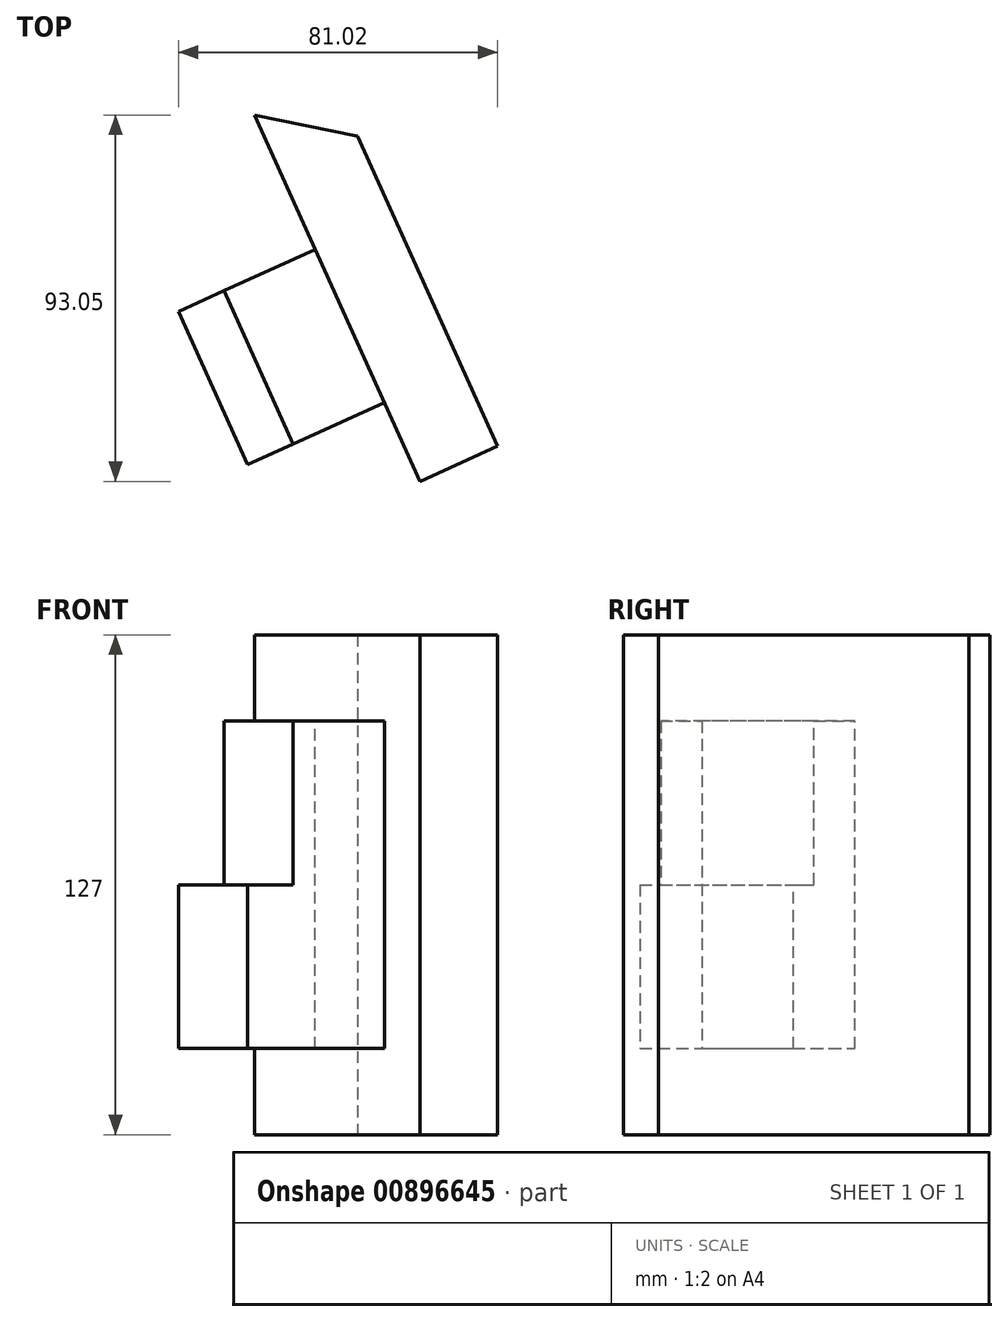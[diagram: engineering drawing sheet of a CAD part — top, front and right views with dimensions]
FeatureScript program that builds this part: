
annotation { "Feature Type Name" : "Feature", "Feature Type Description" : "" }
export const myFeature = defineFeature(function(context is Context, id is Id, definition is map)
    precondition{}
    {
        {
            var Q0;
            Q0=qCreatedBy(makeId("Top.planeOp"),FACE);
            var sketch = newSketch(context, id + "F0", { "sketchPlane" : qUnion([Q0])});
            skLineSegment(sketch, "E0", {"start": v(-10.82, 72.83) * mm, "end": v(31.2, -20.22) * mm});
            skLineSegment(sketch, "E1", {"start": v(31.2, -20.22) * mm, "end": v(50.91, -11.32) * mm});
            skLineSegment(sketch, "E2", {"start": v(50.91, -11.32) * mm, "end": v(15.33, 67.5) * mm});
            skLineSegment(sketch, "E3", {"start": v(15.33, 67.5) * mm, "end": v(-10.82, 72.83) * mm});
            skSolve(sketch);
        }
        {
            var Q0;
            Q0=makeQuery(id+"F0.imprint","IMPRINT",FACE,{"disambiguationData":[TD([[makeQuery(id+"F0.imprint","IMPRINT",EDGE,{"derivedFrom":sQuery(id+"F0.wireOp",EDGE,"E0")}),1.0]])]});
            extrude(context, id + "F1", {"entities" : qUnion([Q0]), "depth" : 127 * mm, "offsetDistance" : 25.4 * mm});
        }
        {
            var Q0;
            Q0=makeQuery(id+"F1.opExtrude","SWEPT_FACE",FACE,{"disambiguationData":[OSD([sQuery(id+"F0.wireOp",EDGE,"E0")])]});
            var sketch = newSketch(context, id + "F2", { "sketchPlane" : qUnion([Q0])});
            skLineSegment(sketch, "E4.0", {"start": v(9.38, 21.9) * mm, "end": v(-33.32, 21.9) * mm});
            skLineSegment(sketch, "E4.1", {"start": v(9.38, 105.1) * mm, "end": v(9.38, 21.9) * mm});
            skLineSegment(sketch, "E4.2", {"start": v(-33.32, 105.1) * mm, "end": v(9.38, 105.1) * mm});
            skLineSegment(sketch, "E4.3", {"start": v(-33.32, 21.9) * mm, "end": v(-33.32, 105.1) * mm});
            skSolve(sketch);
        }
        {
            var Q0;
            Q0=makeQuery(id+"F2.imprint","IMPRINT",FACE,{"disambiguationData":[TD([[makeQuery(id+"F2.imprint","IMPRINT",EDGE,{"derivedFrom":sQuery(id+"F2.wireOp",EDGE,"E4.0")}),-1.0]])]});
            extrude(context, id + "F3", {"entities" : qUnion([Q0]), "operationType" : NewBodyOperationType.ADD, "depth" : 25.4 * mm, "offsetDistance" : 25.4 * mm});
        }
        {
            var Q0;
            Q0=makeQuery(id+"F3.opExtrude","CAP_FACE",FACE,{"disambiguationData":[OSD([sQuery(id+"F2.wireOp",EDGE,"E4.0"),sQuery(id+"F2.wireOp",EDGE,"E4.1"),sQuery(id+"F2.wireOp",EDGE,"E4.2"),sQuery(id+"F2.wireOp",EDGE,"E4.3")])],"isStart":false});
            var sketch = newSketch(context, id + "F4", { "sketchPlane" : qUnion([Q0])});
            skLineSegment(sketch, "E5", {"start": v(9.38, 63.5) * mm, "end": v(-33.32, 63.5) * mm});
            skSolve(sketch);
        }
        {
            var Q0;
            {var subQ0=sQuery(id+"F4.wireOp",EDGE,"E5");Q0=makeQuery(id+"F4.imprint","IMPRINT",FACE,{"disambiguationData":[TD([[makeQuery(id+"F4.imprint","IMPRINT",EDGE,{"derivedFrom":subQ0}),1.0]])]});}
            extrude(context, id + "F5", {"entities" : qUnion([Q0]), "operationType" : NewBodyOperationType.ADD, "depth" : 12.7 * mm, "offsetDistance" : 25.4 * mm});
        }
    });
